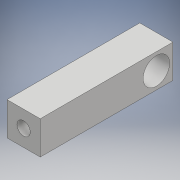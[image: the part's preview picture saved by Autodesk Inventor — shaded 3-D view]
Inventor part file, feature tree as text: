
AUTODESK INVENTOR PART (.ipt)
format: ipt  version: 2017 SP1 (Build 210196100, 196)  size: 223,232 bytes
history: native  units: mm
features: sketch x3, hole x2, extrude x1
ambient origin geometry x8: Origin, YZ Plane, XZ Plane, XY Plane, X Axis, Y Axis, Z Axis, Center Point
bodies: Solide1 (feature_tree)
feature tree (6):
  extrude  "Extrusion1"  Depth=10.0mm
  hole  "Perçage1"  [1 undecoded]
  hole  "Perçage2"  [1 undecoded]
  sketch  "Esquisse1"
  sketch  "Esquisse2"
  sketch  "Esquisse3"
note: 2 required parameter values undecoded (feature->parameter linkage not recoverable at this tier; creation-order binding heuristic only, values carry confidence <= 0.55)
